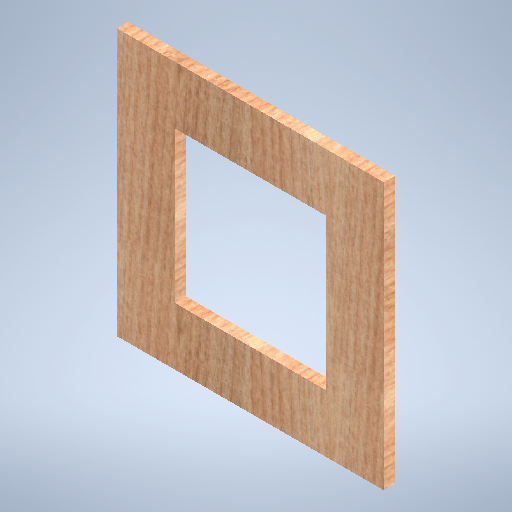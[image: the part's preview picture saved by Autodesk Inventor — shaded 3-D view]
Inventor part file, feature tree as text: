
AUTODESK INVENTOR PART (.ipt)
format: ipt  version: 2025.1 (Build 291241000, 241)  size: 398,848 bytes
history: native  units: in
note: dims shown in document units (in); Inventor stores cm internally (conversion verified against a paired STEP export)
features: extrude x1, sketch x1
ambient origin geometry x8: Origin, YZ Plane, XZ Plane, XY Plane, X Axis, Y Axis, Z Axis, Center Point
bodies: Solid1 (feature_tree)
feature tree (2):
  extrude  "Extrusion1"  Depth=11.811in
  sketch  "Sketch2"  dims[d0=11.811in d1=11.811in d2=6.6929in d3=6.6929in d4=0.5in d5=0.0in]
